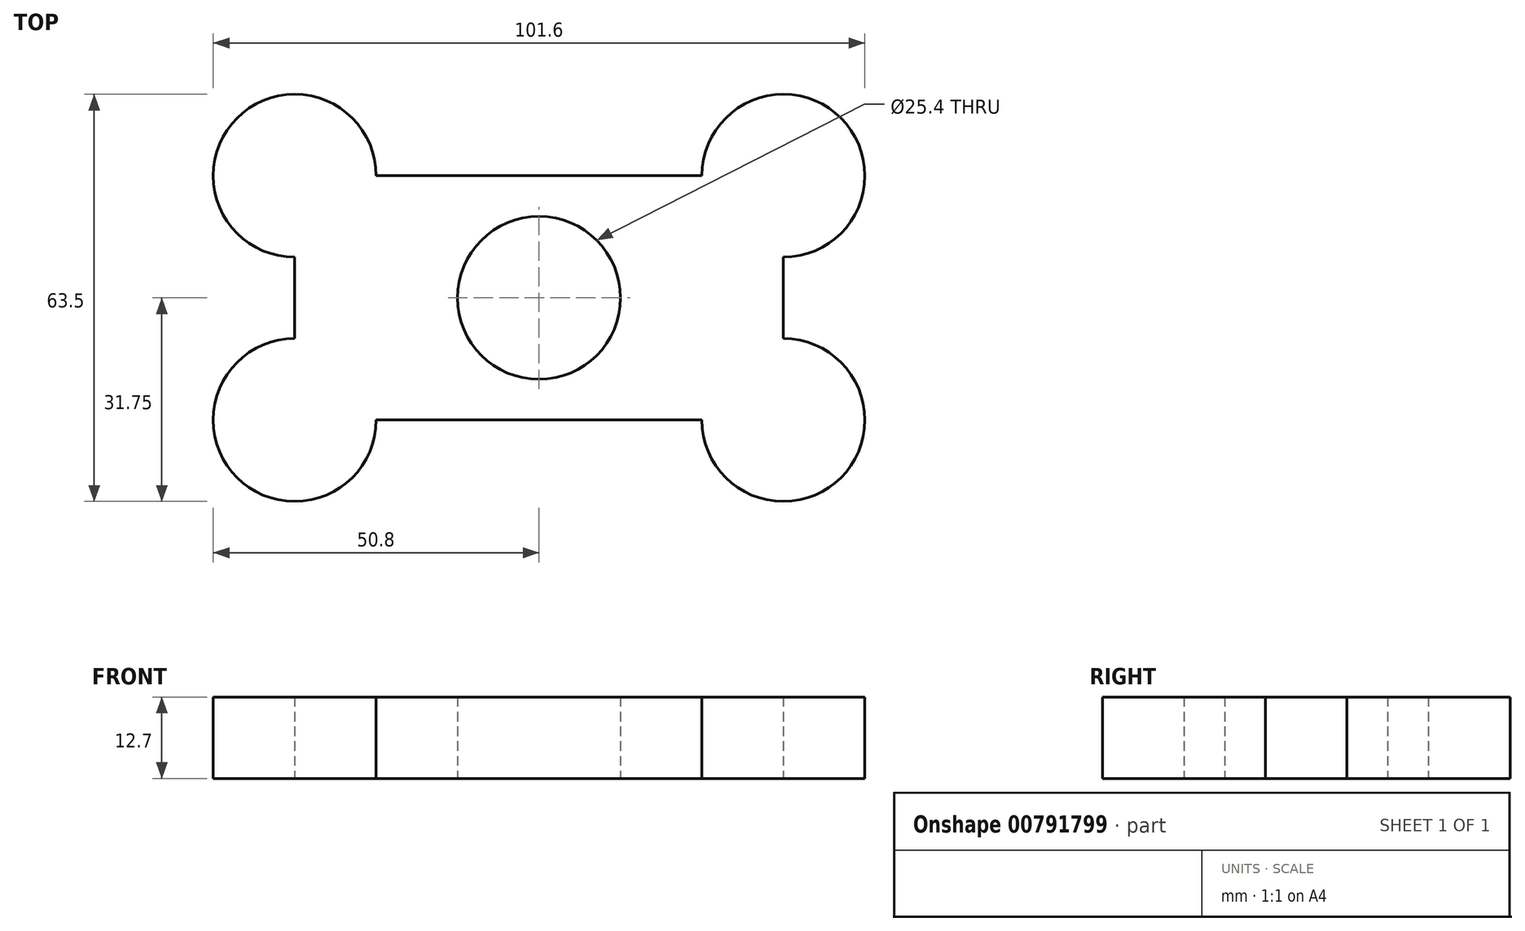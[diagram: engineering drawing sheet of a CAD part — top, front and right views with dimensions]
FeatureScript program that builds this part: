
annotation { "Feature Type Name" : "Feature", "Feature Type Description" : "" }
export const myFeature = defineFeature(function(context is Context, id is Id, definition is map)
    precondition{}
    {
        {
            var Q0;
            Q0=qCreatedBy(makeId("Top.planeOp"),FACE);
            var sketch = newSketch(context, id + "F0", { "sketchPlane" : qUnion([Q0])});
            skLineSegment(sketch, "E0.bottom", {"start": v(-25.4, 19.05) * mm, "end": v(25.4, 19.05) * mm});
            skLineSegment(sketch, "E0.top", {"start": v(-25.4, -19.05) * mm, "end": v(25.4, -19.05) * mm});
            skLineSegment(sketch, "E0.left", {"start": v(-38.1, 6.35) * mm, "end": v(-38.1, -6.35) * mm});
            skLineSegment(sketch, "E0.right", {"start": v(38.1, 6.35) * mm, "end": v(38.1, -6.35) * mm});
            skPoint(sketch, "E0.middle", {"position": v(0, 0) * mm});
            skCircle(sketch, "E1", {"center": v(0, 0) * mm, "radius": 12.7 * mm});
            skArc(sketch, "E2", {"start": v(38.1, 6.35) * mm, "mid": v(47.08, 28.03) * mm, "end": v(25.4, 19.05) * mm});
            skArc(sketch, "E3", {"start": v(25.4, -19.05) * mm, "mid": v(47.08, -28.03) * mm, "end": v(38.1, -6.35) * mm});
            skArc(sketch, "E4", {"start": v(-25.4, 19.05) * mm, "mid": v(-47.08, 28.03) * mm, "end": v(-38.1, 6.35) * mm});
            skArc(sketch, "E5", {"start": v(-38.1, -6.35) * mm, "mid": v(-47.08, -28.03) * mm, "end": v(-25.4, -19.05) * mm});
            skSolve(sketch);
        }
        {
            var Q0;
            Q0=makeQuery(id+"F0.imprint","IMPRINT",FACE,{"disambiguationData":[TD([[makeQuery(id+"F0.imprint","IMPRINT",EDGE,{"derivedFrom":sQuery(id+"F0.wireOp",EDGE,"E0.bottom")}),-1.0]])]});
            extrude(context, id + "F1", {"entities" : qUnion([Q0]), "depth" : 12.7 * mm, "offsetDistance" : 25.4 * mm});
        }
    });
